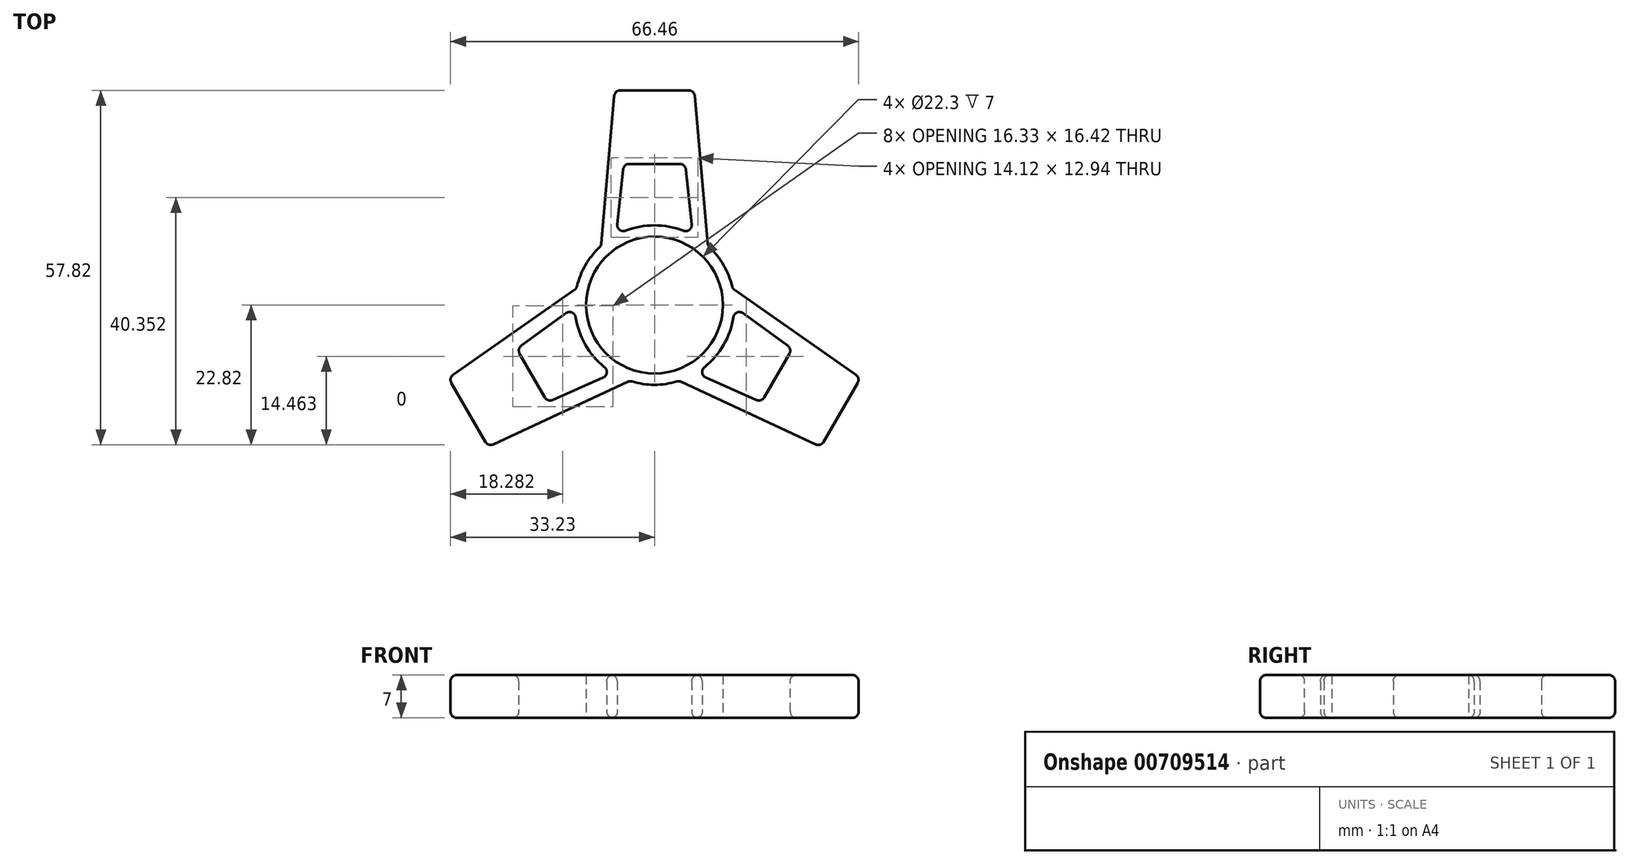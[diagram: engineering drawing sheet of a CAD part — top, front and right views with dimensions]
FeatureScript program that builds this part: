
annotation { "Feature Type Name" : "Feature", "Feature Type Description" : "" }
export const myFeature = defineFeature(function(context is Context, id is Id, definition is map)
    precondition{}
    {
        {
            var Q0;
            Q0=qCreatedBy(makeId("Top.planeOp"),FACE);
            var sketch = newSketch(context, id + "F0", { "sketchPlane" : qUnion([Q0])});
            skCircle(sketch, "E0", {"center": v(0, 0) * mm, "radius": 11.15 * mm});
            skCircle(sketch, "E1", {"center": v(0, 0) * mm, "radius": 13 * mm});
            skLineSegment(sketch, "E2", {"start": v(-8.7, 9.66) * mm, "end": v(-6.48, 35) * mm});
            skLineSegment(sketch, "E3", {"start": v(-6.48, 35) * mm, "end": v(0, 35) * mm});
            skLineSegment(sketch, "E4", {"start": v(-6.25, 11.4) * mm, "end": v(-5.02, 23) * mm});
            skLineSegment(sketch, "E5", {"start": v(-5.02, 23) * mm, "end": v(0, 23) * mm});
            skLineSegment(sketch, "E6.MirrorCS", {"start": v(6.48, 35) * mm, "end": v(0, 35) * mm});
            skLineSegment(sketch, "E7.MirrorCS", {"start": v(8.7, 9.66) * mm, "end": v(6.48, 35) * mm});
            skLineSegment(sketch, "E8.MirrorCS", {"start": v(6.25, 11.4) * mm, "end": v(5.02, 23) * mm});
            skLineSegment(sketch, "E9.MirrorCS", {"start": v(5.02, 23) * mm, "end": v(0, 23) * mm});
            skLineSegment(sketch, "E10.1.0", {"start": v(-27.07, -23.11) * mm, "end": v(-30.31, -17.5) * mm});
            skLineSegment(sketch, "E10.1.1", {"start": v(-4.02, -12.36) * mm, "end": v(-27.07, -23.11) * mm});
            skLineSegment(sketch, "E10.1.2", {"start": v(-17.4, -15.85) * mm, "end": v(-19.92, -11.5) * mm});
            skLineSegment(sketch, "E10.1.3", {"start": v(-6.75, -11.11) * mm, "end": v(-17.4, -15.85) * mm});
            skLineSegment(sketch, "E10.1.6", {"start": v(-33.55, -11.89) * mm, "end": v(-30.31, -17.5) * mm});
            skLineSegment(sketch, "E10.1.7", {"start": v(-12.72, 2.7) * mm, "end": v(-33.55, -11.89) * mm});
            skLineSegment(sketch, "E10.1.8", {"start": v(-13, -0.29) * mm, "end": v(-22.43, -7.15) * mm});
            skLineSegment(sketch, "E10.1.9", {"start": v(-22.43, -7.15) * mm, "end": v(-19.92, -11.5) * mm});
            skLineSegment(sketch, "E10.2.0", {"start": v(33.55, -11.89) * mm, "end": v(30.31, -17.5) * mm});
            skLineSegment(sketch, "E10.2.1", {"start": v(12.72, 2.7) * mm, "end": v(33.55, -11.89) * mm});
            skLineSegment(sketch, "E10.2.2", {"start": v(22.43, -7.15) * mm, "end": v(19.92, -11.5) * mm});
            skLineSegment(sketch, "E10.2.3", {"start": v(13, -0.29) * mm, "end": v(22.43, -7.15) * mm});
            skLineSegment(sketch, "E10.2.6", {"start": v(27.07, -23.11) * mm, "end": v(30.31, -17.5) * mm});
            skLineSegment(sketch, "E10.2.7", {"start": v(4.02, -12.36) * mm, "end": v(27.07, -23.11) * mm});
            skLineSegment(sketch, "E10.2.8", {"start": v(6.75, -11.11) * mm, "end": v(17.4, -15.85) * mm});
            skLineSegment(sketch, "E10.2.9", {"start": v(17.4, -15.85) * mm, "end": v(19.92, -11.5) * mm});
            skSolve(sketch);
        }
        {
            var Q0;
            Q0 = qSketchRegion(id + "F0", true);
            extrude(context, id + "F1", {"entities" : qUnion([Q0]), "depth" : 7 * mm, "offsetDistance" : 25 * mm});
        }
        {
            var Q0;
            Q0=makeQuery(id+"F1.opExtrude","SWEPT_FACE",FACE,{"disambiguationData":[OSD([sQuery(id+"F0.wireOp",EDGE,"E10.1.1")])]});
            var Q1;
            {var subQ0=sQuery(id+"F0.wireOp",EDGE,"E1");Q1=makeQuery(id+"F1.opExtrude","SWEPT_FACE",FACE,{"disambiguationData":[OSD([subQ0]),TDD([makeQuery(id+"F0.imprint","IMPRINT",EDGE,{"disambiguationData":[TD([[makeQuery(id+"F0.imprint","INTERSECT",VERTEX,{"derivedFrom":[sQuery(id+"F0.wireOp",EDGE,"E10.1.1"),subQ0]}),-1.0]])],"derivedFrom":subQ0})])]});}
            var Q2;
            Q2=makeQuery(id+"F1.opExtrude","SWEPT_FACE",FACE,{"disambiguationData":[OSD([sQuery(id+"F0.wireOp",EDGE,"E10.2.7")])]});
            var Q3;
            Q3=makeQuery(id+"F1.opExtrude","SWEPT_FACE",FACE,{"disambiguationData":[OSD([sQuery(id+"F0.wireOp",EDGE,"E10.2.0"),sQuery(id+"F0.wireOp",EDGE,"E10.2.6")])]});
            var Q4;
            Q4=makeQuery(id+"F1.opExtrude","SWEPT_FACE",FACE,{"disambiguationData":[OSD([sQuery(id+"F0.wireOp",EDGE,"E10.2.1")])]});
            var Q5;
            {var subQ0=sQuery(id+"F0.wireOp",EDGE,"E1");Q5=makeQuery(id+"F1.opExtrude","SWEPT_FACE",FACE,{"disambiguationData":[OSD([subQ0]),TDD([makeQuery(id+"F0.imprint","IMPRINT",EDGE,{"disambiguationData":[TD([[makeQuery(id+"F0.imprint","INTERSECT",VERTEX,{"derivedFrom":[sQuery(id+"F0.wireOp",EDGE,"E7.MirrorCS"),subQ0]}),1.0]])],"derivedFrom":subQ0})])]});}
            var Q6;
            Q6=makeQuery(id+"F1.opExtrude","SWEPT_FACE",FACE,{"disambiguationData":[OSD([sQuery(id+"F0.wireOp",EDGE,"E7.MirrorCS")])]});
            var Q7;
            Q7=makeQuery(id+"F1.opExtrude","SWEPT_FACE",FACE,{"disambiguationData":[OSD([sQuery(id+"F0.wireOp",EDGE,"E3"),sQuery(id+"F0.wireOp",EDGE,"E6.MirrorCS")])]});
            var Q8;
            Q8=makeQuery(id+"F1.opExtrude","SWEPT_FACE",FACE,{"disambiguationData":[OSD([sQuery(id+"F0.wireOp",EDGE,"E2")])]});
            var Q9;
            {var subQ0=sQuery(id+"F0.wireOp",EDGE,"E1");Q9=makeQuery(id+"F1.opExtrude","SWEPT_FACE",FACE,{"disambiguationData":[OSD([subQ0]),TDD([makeQuery(id+"F0.imprint","IMPRINT",EDGE,{"disambiguationData":[TD([[makeQuery(id+"F0.imprint","INTERSECT",VERTEX,{"derivedFrom":[sQuery(id+"F0.wireOp",EDGE,"E2"),subQ0]}),-1.0]])],"derivedFrom":subQ0})])]});}
            var Q10;
            Q10=makeQuery(id+"F1.opExtrude","SWEPT_FACE",FACE,{"disambiguationData":[OSD([sQuery(id+"F0.wireOp",EDGE,"E10.1.7")])]});
            var Q11;
            Q11=makeQuery(id+"F1.opExtrude","SWEPT_FACE",FACE,{"disambiguationData":[OSD([sQuery(id+"F0.wireOp",EDGE,"E10.1.0"),sQuery(id+"F0.wireOp",EDGE,"E10.1.6")])]});
            var Q12;
            {var subQ0=sQuery(id+"F0.wireOp",EDGE,"E1");Q12=makeQuery(id+"F1.opExtrude","SWEPT_FACE",FACE,{"disambiguationData":[OSD([subQ0]),TDD([makeQuery(id+"F0.imprint","IMPRINT",EDGE,{"disambiguationData":[TD([[makeQuery(id+"F0.imprint","INTERSECT",VERTEX,{"derivedFrom":[sQuery(id+"F0.wireOp",EDGE,"E10.2.3"),subQ0]}),1.0]])],"derivedFrom":subQ0})])]});}
            var Q13;
            Q13=makeQuery(id+"F1.opExtrude","SWEPT_FACE",FACE,{"disambiguationData":[OSD([sQuery(id+"F0.wireOp",EDGE,"E10.2.3")])]});
            var Q14;
            Q14=makeQuery(id+"F1.opExtrude","SWEPT_FACE",FACE,{"disambiguationData":[OSD([sQuery(id+"F0.wireOp",EDGE,"E10.2.2"),sQuery(id+"F0.wireOp",EDGE,"E10.2.9")])]});
            var Q15;
            Q15=makeQuery(id+"F1.opExtrude","SWEPT_FACE",FACE,{"disambiguationData":[OSD([sQuery(id+"F0.wireOp",EDGE,"E10.2.8")])]});
            var Q16;
            Q16=makeQuery(id+"F1.opExtrude","SWEPT_FACE",FACE,{"disambiguationData":[OSD([sQuery(id+"F0.wireOp",EDGE,"E5"),sQuery(id+"F0.wireOp",EDGE,"E9.MirrorCS")])]});
            var Q17;
            Q17=makeQuery(id+"F1.opExtrude","SWEPT_FACE",FACE,{"disambiguationData":[OSD([sQuery(id+"F0.wireOp",EDGE,"E8.MirrorCS")])]});
            var Q18;
            Q18=makeQuery(id+"F1.opExtrude","SWEPT_FACE",FACE,{"disambiguationData":[OSD([sQuery(id+"F0.wireOp",EDGE,"E4")])]});
            var Q19;
            {var subQ0=sQuery(id+"F0.wireOp",EDGE,"E1");Q19=makeQuery(id+"F1.opExtrude","SWEPT_FACE",FACE,{"disambiguationData":[OSD([subQ0]),TDD([makeQuery(id+"F0.imprint","IMPRINT",EDGE,{"disambiguationData":[TD([[makeQuery(id+"F0.imprint","INTERSECT",VERTEX,{"derivedFrom":[sQuery(id+"F0.wireOp",EDGE,"E4"),subQ0]}),1.0]])],"derivedFrom":subQ0})])]});}
            var Q20;
            {var subQ0=sQuery(id+"F0.wireOp",EDGE,"E1");Q20=makeQuery(id+"F1.opExtrude","SWEPT_FACE",FACE,{"disambiguationData":[OSD([subQ0]),TDD([makeQuery(id+"F0.imprint","IMPRINT",EDGE,{"disambiguationData":[TD([[makeQuery(id+"F0.imprint","INTERSECT",VERTEX,{"derivedFrom":[sQuery(id+"F0.wireOp",EDGE,"E10.1.3"),subQ0]}),1.0]])],"derivedFrom":subQ0})])]});}
            var Q21;
            Q21=makeQuery(id+"F1.opExtrude","SWEPT_FACE",FACE,{"disambiguationData":[OSD([sQuery(id+"F0.wireOp",EDGE,"E10.1.8")])]});
            var Q22;
            Q22=makeQuery(id+"F1.opExtrude","SWEPT_FACE",FACE,{"disambiguationData":[OSD([sQuery(id+"F0.wireOp",EDGE,"E10.1.2"),sQuery(id+"F0.wireOp",EDGE,"E10.1.9")])]});
            var Q23;
            Q23=makeQuery(id+"F1.opExtrude","SWEPT_FACE",FACE,{"disambiguationData":[OSD([sQuery(id+"F0.wireOp",EDGE,"E10.1.3")])]});
            fillet(context, id + "F2", {"entities" : qUnion([Q0, Q1, Q2, Q3, Q4, Q5, Q6, Q7, Q8, Q9, Q10, Q11, Q12, Q13, Q14, Q15, Q16, Q17, Q18, Q19, Q20, Q21, Q22, Q23]), "radius" : 1 * mm, "tangentPropagation" : true, "allowEdgeOverflow" : false});
        }
    });
